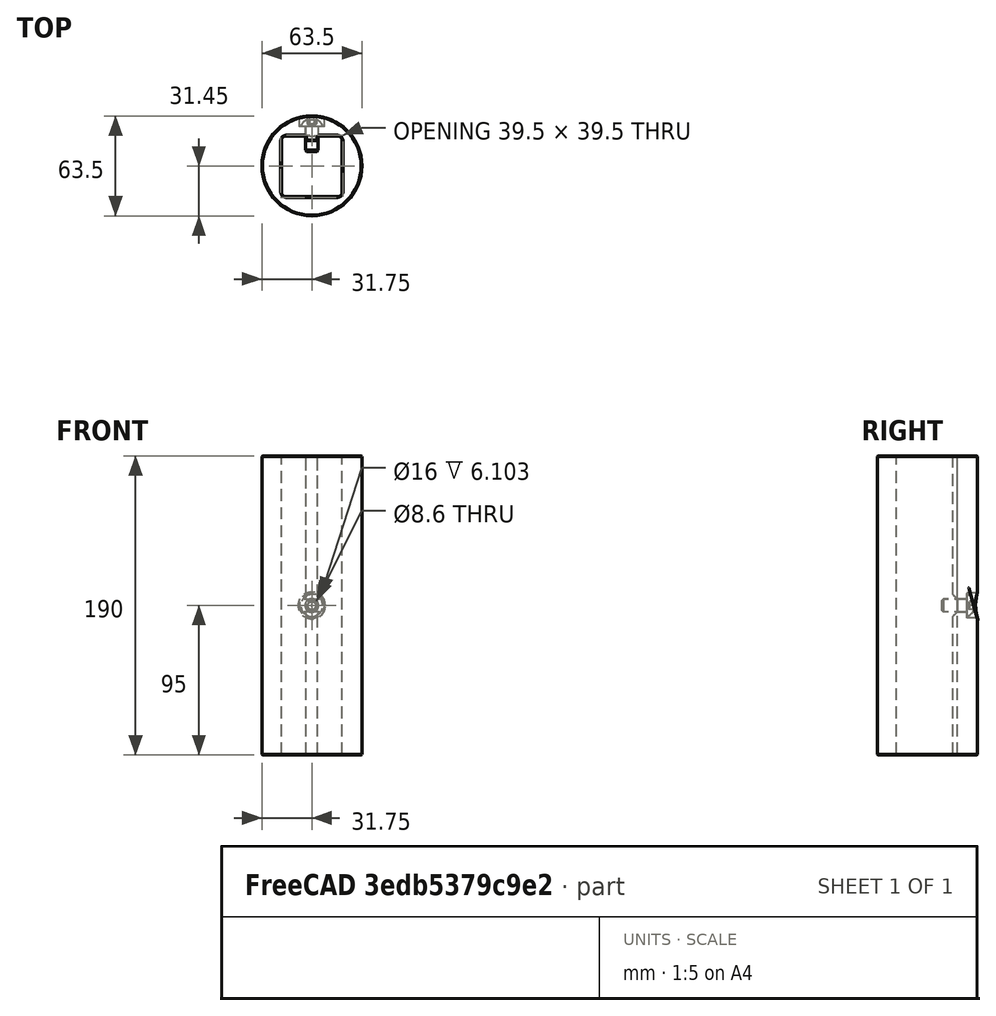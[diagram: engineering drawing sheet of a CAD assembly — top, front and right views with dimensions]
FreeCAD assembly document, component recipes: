
FREECAD ASSEMBLY — COMPONENT RECIPES ("bar-cover")

This assembly document has 3 components, labeled P0..P2 below (a component is one placed body or linked part). 2 of them carry a construction recipe — the FreeCAD feature program that regenerates the part from scratch, quoted from this document or its linked companion documents; the rest are supplied as boundary geometry only. No exploded tour is included for this assembly.
COMPONENT P0 — recipe-attached ("Bar Cover", modeled in this document).
Construction recipe (the document's own serialized feature program — sketch geometry with constraints, then the solid features built on it; lengths are millimeters unless a unit is written):

FEATURE [Sketcher::SketchObject] Sketch
  FullyConstrained = true
  MapMode = 5
  Support = -> [XY_Plane]
  expr: Constraints[19] = <<Configuration>>.extrusion_width + Spreadsheet.fit_tolerance * 2
  expr: Constraints[1] = <<Configuration>>.cover_outer_diameter
  expr: Constraints[28] = <<Configuration>>.slot_width - <<Configuration>>.fit_tolerance * 2
  expr: Constraints[36] = <<Configuration>>.slot_aligner_height
  expr: Constraints[39] = <<Configuration>>.extrusion_width / 2 + <<Configuration>>.fit_tolerance * 2
  expr: Constraints[40] = <<Configuration>>.extrusion_width / 2
  expr: Constraints[41] = <<Configuration>>.extrusion_corner_radius
  expr: Constraints[42] = <<Configuration>>.slot_corner_radius
  sketch-geometry (19):
    g0: Circle CenterX=0 CenterY=0 CenterZ=0 NormalX=0 NormalY=0 NormalZ=1 AngleXU=0 Radius=31.75
    g1: ArcOfCircle CenterX=-16.175 CenterY=15.875 CenterZ=0 NormalX=0 NormalY=0 NormalZ=1 AngleXU=0 Radius=3.175 StartAngle=1.5708 EndAngle=3.14159
    g2: LineSegment StartX=-16.175 StartY=19.05 StartZ=0 EndX=-5.035 EndY=19.05 EndZ=0
    g3: ArcOfCircle CenterX=16.175 CenterY=15.875 CenterZ=0 NormalX=0 NormalY=0 NormalZ=1 AngleXU=0 Radius=3.175 StartAngle=3e-16 EndAngle=1.5708
    g4: LineSegment StartX=19.35 StartY=15.875 StartZ=0 EndX=19.35 EndY=-16.475 EndZ=0
    g5: ArcOfCircle CenterX=16.175 CenterY=-16.475 CenterZ=0 NormalX=0 NormalY=0 NormalZ=1 AngleXU=0 Radius=3.175 StartAngle=4.71239 EndAngle=6.28319
    g6: LineSegment StartX=16.175 StartY=-19.65 StartZ=0 EndX=-16.175 EndY=-19.65 EndZ=0
    g7: ArcOfCircle CenterX=-16.175 CenterY=-16.475 CenterZ=0 NormalX=0 NormalY=0 NormalZ=1 AngleXU=0 Radius=3.175 StartAngle=3.14159 EndAngle=4.71239
    g8: LineSegment StartX=-19.35 StartY=-16.475 StartZ=0 EndX=-19.35 EndY=15.875 EndZ=0
    g9: GeomPoint X=-19.35 Y=19.05 Z=0
    g10: GeomPoint X=19.35 Y=-19.65 Z=0
    g11: LineSegment StartX=-3.765 StartY=17.78 StartZ=0 EndX=-3.765 EndY=17.05 EndZ=0
    g12: LineSegment StartX=-2.765 StartY=16.05 StartZ=0 EndX=2.765 EndY=16.05 EndZ=0
    g13: LineSegment StartX=3.765 StartY=17.05 StartZ=0 EndX=3.765 EndY=17.78 EndZ=0
    g14: LineSegment StartX=5.035 StartY=19.05 StartZ=0 EndX=16.175 EndY=19.05 EndZ=0
    g15: ArcOfCircle CenterX=-5.035 CenterY=17.78 CenterZ=0 NormalX=0 NormalY=0 NormalZ=1 AngleXU=0 Radius=1.27 StartAngle=7e-16 EndAngle=1.5708
    g16: ArcOfCircle CenterX=5.035 CenterY=17.78 CenterZ=0 NormalX=0 NormalY=0 NormalZ=1 AngleXU=0 Radius=1.27 StartAngle=1.5708 EndAngle=3.14159
    g17: ArcOfCircle CenterX=-2.765 CenterY=17.05 CenterZ=0 NormalX=0 NormalY=0 NormalZ=1 AngleXU=0 Radius=1 StartAngle=3.14159 EndAngle=4.71239
    g18: ArcOfCircle CenterX=2.765 CenterY=17.05 CenterZ=0 NormalX=0 NormalY=0 NormalZ=1 AngleXU=0 Radius=1 StartAngle=4.71239 EndAngle=6.28319
  constraints (43):
    c: Coincident(g0,g-1)
    c: Diameter(g0) = 63.5
    c: Tangent(g1,g2) = 1.5708
    c: Tangent(g3,g4) = 1.5708
    c: Tangent(g4,g5) = 1.5708
    c: Tangent(g5,g6) = 1.5708
    c: Tangent(g6,g7) = 1.5708
    c: Tangent(g7,g8) = 1.5708
    c: Tangent(g8,g1) = 1.5708
    c: Horizontal(g2)
    c: Horizontal(g6)
    c: Vertical(g4)
    c: Vertical(g8)
    c: Equal(g3,g5)
    c: Equal(g5,g7)
    c: PointOnObject(g9,g2)
    c: PointOnObject(g9,g8)
    c: PointOnObject(g10,g4)
    c: PointOnObject(g10,g6)
    c: DistanceX(g1,g3) = 38.7
    c: Vertical(g11)
    c: Vertical(g13)
    c: Tangent(g11,g15) = 1.5708
    c: Tangent(g2,g15) = 1.5708
    c: Tangent(g13,g16) = 1.5708
    c: Tangent(g14,g16) = 1.5708
    c: Equal(g16,g15)
    c: Tangent(g14,g2)
    c: DistanceX(g11,g13) = 7.53
    c: Tangent(g12,g17) = -1.5708
    c: Tangent(g11,g17) = -1.5708
    c: Tangent(g12,g18) = -1.5708
    c: Tangent(g13,g18) = -1.5708
    c: Equal(g17,g18)
    c: Diameter(g17) = 2
    c: Symmetric(g11,g13,g-2)
    c: DistanceY(g12,g2) = 3
    c: Tangent(g14,g3) = 1.5708
    c: Symmetric(g1,g3,g-2)
    c: DistanceY(g6,g-1) = 19.65
    c: DistanceY(g-1,g3) = 19.05
    c: Radius(g3) = 3.175
    c: Radius(g15) = 1.27
FEATURE [PartDesign::Pad] Pad
  Direction = (0,0,1)
  Length = 190
  Length2 = 10
  Profile = -> Sketch
  ReferenceAxis = -> Sketch [N_Axis]
  Type = 0
  expr: Length = <<Configuration>>.cover_length
FEATURE [Sketcher::SketchObject] Sketch001
  AttachmentOffset = pos=(0,0,-25.05) rot=(0,0,1;0rad)
  FullyConstrained = true
  MapMode = 5
  Placement = pos=(0,25.05,5.6e-15) rot=(1,0,0;1.5708rad)
  Support = -> [XZ_Plane]
  expr: .AttachmentOffset.Base.z = -(<<Configuration>>.extrusion_width / 2) - 6 mm
  expr: Constraints[1] = <<Configuration>>.screw_offset
  sketch-geometry (1):
    g0: Circle CenterX=0 CenterY=95 CenterZ=0 NormalX=0 NormalY=0 NormalZ=1 AngleXU=0 Radius=8
  constraints (3):
    c: PointOnObject(g0,g-2)
    c: DistanceY(g-1,g0) = 95
    c: Diameter(g0) = 16
FEATURE [PartDesign::Pocket] Pocket
  BaseFeature = -> Pad
  Direction = (0,1,2e-16)
  Length = 6.2
  Length2 = 5
  Profile = -> Sketch001
  ReferenceAxis = -> Sketch001 [N_Axis]
  Type = 1
FEATURE [Sketcher::SketchObject] Sketch002
  FullyConstrained = true
  MapMode = 5
  Placement = pos=(0,0,0) rot=(1,0,0;1.5708rad)
  Support = -> [XZ_Plane]
  expr: Constraints[1] = <<Configuration>>.screw_offset
  expr: Constraints[2] = 8 mm + <<Configuration>>.fit_tolerance * 2
  sketch-geometry (1):
    g0: Circle CenterX=0 CenterY=95 CenterZ=0 NormalX=0 NormalY=0 NormalZ=1 AngleXU=0 Radius=4.3
  constraints (3):
    c: PointOnObject(g0,g-2)
    c: DistanceY(g-1,g0) = 95
    c: Diameter(g0) = 8.6
FEATURE [PartDesign::Pocket] Pocket001
  BaseFeature = -> Pocket
  Direction = (0,1,2e-16)
  Length = 5
  Length2 = 5
  Profile = -> Sketch002
  ReferenceAxis = -> Sketch002 [N_Axis]
  Type = 1
FEATURE [Sketcher::SketchObject] Sketch003
  AttachmentOffset = pos=(0,19.05,95) rot=(-1,0,0;1.5708rad)
  FullyConstrained = true
  MapMode = 5
  Placement = pos=(0,19.05,95) rot=(-1,0,0;1.5708rad)
  Support = -> [XY_Plane]
  expr: .AttachmentOffset.Base.y = <<Configuration>>.extrusion_width / 2
  expr: .AttachmentOffset.Base.z = <<Configuration>>.screw_offset
  sketch-geometry (5):
    g0: LineSegment StartX=6 StartY=-4 StartZ=0 EndX=6 EndY=4 EndZ=0
    g1: LineSegment StartX=6 StartY=4 StartZ=0 EndX=-6 EndY=4 EndZ=0
    g2: LineSegment StartX=-6 StartY=4 StartZ=0 EndX=-6 EndY=-4 EndZ=0
    g3: LineSegment StartX=-6 StartY=-4 StartZ=0 EndX=6 EndY=-4 EndZ=0
    g4: GeomPoint X=0 Y=0 Z=0
  constraints (12):
    c: Coincident(g0,g1)
    c: Coincident(g1,g2)
    c: Coincident(g2,g3)
    c: Coincident(g3,g0)
    c: Horizontal(g1)
    c: Horizontal(g3)
    c: Vertical(g0)
    c: Vertical(g2)
    c: Symmetric(g1,g0,g4)
    c: Coincident(g4,g-1)
    c: DistanceX(g1,g1) = 12
    c: DistanceY(g2,g2) = 8
FEATURE [Sketcher::SketchObject] Sketch004
  AttachmentOffset = pos=(0,15.05,95) rot=(-1,0,0;1.5708rad)
  FullyConstrained = true
  MapMode = 5
  Placement = pos=(0,15.05,95) rot=(-1,0,0;1.5708rad)
  Support = -> [XY_Plane]
  expr: .AttachmentOffset.Base.y = <<Configuration>>.extrusion_width / 2 - <<Configuration>>.slot_aligner_height - 1 mm
  expr: .AttachmentOffset.Base.z = <<Configuration>>.screw_offset
  sketch-geometry (5):
    g0: LineSegment StartX=6 StartY=-8 StartZ=0 EndX=6 EndY=8 EndZ=0
    g1: LineSegment StartX=6 StartY=8 StartZ=0 EndX=-6 EndY=8 EndZ=0
    g2: LineSegment StartX=-6 StartY=8 StartZ=0 EndX=-6 EndY=-8 EndZ=0
    g3: LineSegment StartX=-6 StartY=-8 StartZ=0 EndX=6 EndY=-8 EndZ=0
    g4: GeomPoint X=0 Y=0 Z=0
  constraints (12):
    c: Coincident(g0,g1)
    c: Coincident(g1,g2)
    c: Coincident(g2,g3)
    c: Coincident(g3,g0)
    c: Horizontal(g1)
    c: Horizontal(g3)
    c: Vertical(g0)
    c: Vertical(g2)
    c: Symmetric(g1,g0,g4)
    c: Coincident(g4,g-1)
    c: DistanceX(g1,g1) = 12
    c: DistanceY(g2,g2) = 16
FEATURE [PartDesign::SubtractiveLoft] SubtractiveLoft
  BaseFeature = -> Pocket001
  Closed = false
  Profile = -> Sketch003
  Refine = true
  Ruled = false
  Sections = -> [Sketch004]
FEATURE [PartDesign::Chamfer] Chamfer
  Angle = 45
  Base = -> SubtractiveLoft [Face2,Face3]
  BaseFeature = -> SubtractiveLoft
  ChamferType = 0
  FlipDirection = false
  Refine = true
  Size = 0.4
  Size2 = 1
  SupportTransform = false
  UseAllEdges = false
FEATURE [PartDesign::Fillet] Fillet
  Base = -> Chamfer [Edge4]
  BaseFeature = -> Chamfer
  Radius = 0.6
  Refine = true
  SupportTransform = false
  UseAllEdges = false
FEATURE [PartDesign::Body] Body  label="BarCover"
  Group = -> [Sketch,Pad,Sketch001,Pocket,Sketch002,Pocket001,Sketch003,Sketch004,SubtractiveLoft,Chamfer,Fillet]
  Origin = -> Origin
  Tip = -> Fillet
COMPONENT P1 — recipe-attached ("1515 33.375", a linked part whose construction recipe lives in a companion FreeCAD document of the same project; that document's serialized recipe follows).
Construction recipe (the companion document, serialized — sketch geometry with constraints, then the solid features built on it; lengths are millimeters unless a unit is written):

FCSTD DOCUMENT  (FreeCAD 0.21R33668 +7 (Git))
Label: 1515-33.375
License: All rights reserved
LicenseURL: http://en.wikipedia.org/wiki/All_rights_reserved
objects: Sketcher::SketchObject×2, PartDesign::CoordinateSystem×1, PartDesign::Pad×1, PartDesign::Pocket×1, PartDesign::PolarPattern×1, PartDesign::Body×1, App::Part×1
note: 9 computed .brp shape members not serialized (recipe doc carries the construction recipe); baked Part::Feature solids carry a one-line shape summary decoded from their .brp

FEATURE [PartDesign::CoordinateSystem] LCS_001
  AttacherType = Attacher::AttachEngine3D
  MapMode = 2
  Support = -> [X_Axis001]
FEATURE [Sketcher::SketchObject] Sketch
  FullyConstrained = true
  MapMode = 5
  Placement = pos=(0,0,0) rot=(1,0,0;1.5708rad)
  Support = -> [XZ_Plane001]
  sketch-geometry (43):
    g0: ArcOfCircle CenterX=-15.87 CenterY=15.87 CenterZ=0 NormalX=0 NormalY=0 NormalZ=1 AngleXU=0 Radius=3.18 StartAngle=1.5708 EndAngle=3.14159
    g1: LineSegment StartX=-15.87 StartY=19.05 StartZ=0 EndX=15.87 EndY=19.05 EndZ=0
    g2: ArcOfCircle CenterX=15.87 CenterY=15.87 CenterZ=0 NormalX=0 NormalY=0 NormalZ=1 AngleXU=0 Radius=3.18 StartAngle=1e-16 EndAngle=1.5708
    g3: LineSegment StartX=19.05 StartY=15.87 StartZ=0 EndX=19.05 EndY=-15.87 EndZ=0
    g4: ArcOfCircle CenterX=15.87 CenterY=-15.87 CenterZ=0 NormalX=0 NormalY=0 NormalZ=1 AngleXU=0 Radius=3.18 StartAngle=4.71239 EndAngle=6.28319
    g5: LineSegment StartX=15.87 StartY=-19.05 StartZ=0 EndX=-15.87 EndY=-19.05 EndZ=0
    g6: ArcOfCircle CenterX=-15.87 CenterY=-15.87 CenterZ=0 NormalX=0 NormalY=0 NormalZ=1 AngleXU=0 Radius=3.18 StartAngle=3.14159 EndAngle=4.71239
    g7: LineSegment StartX=-19.05 StartY=-15.87 StartZ=0 EndX=-19.05 EndY=15.87 EndZ=0
    g8: GeomPoint X=-19.05 Y=19.05 Z=0
    g9: GeomPoint X=19.05 Y=-19.05 Z=0
    g10: LineSegment StartX=-12.145 StartY=-11.895 StartZ=0 EndX=-17.025 EndY=-11.895 EndZ=0
    g11: LineSegment StartX=-17.275 StartY=-12.145 StartZ=0 EndX=-17.275 EndY=-14.485 EndZ=0
    g12: LineSegment StartX=-14.485 StartY=-17.275 StartZ=0 EndX=-12.145 EndY=-17.275 EndZ=0
    g13: LineSegment StartX=-11.895 StartY=-17.025 StartZ=0 EndX=-11.895 EndY=-12.145 EndZ=0
    g14: ArcOfCircle CenterX=-14.485 CenterY=-14.485 CenterZ=0 NormalX=0 NormalY=0 NormalZ=1 AngleXU=0 Radius=2.79 StartAngle=3.14159 EndAngle=4.71239
    g15: LineSegment StartX=-12.145 StartY=11.895 StartZ=0 EndX=-17.025 EndY=11.895 EndZ=0
    g16: LineSegment StartX=-17.275 StartY=12.145 StartZ=0 EndX=-17.275 EndY=14.485 EndZ=0
    g17: ArcOfCircle CenterX=-14.485 CenterY=14.485 CenterZ=0 NormalX=0 NormalY=0 NormalZ=1 AngleXU=0 Radius=2.79 StartAngle=1.5708 EndAngle=3.14159
    g18: LineSegment StartX=-14.485 StartY=17.275 StartZ=0 EndX=-12.145 EndY=17.275 EndZ=0
    g19: LineSegment StartX=-11.895 StartY=17.025 StartZ=0 EndX=-11.895 EndY=12.145 EndZ=0
    g20: LineSegment StartX=12.145 StartY=11.895 StartZ=0 EndX=17.025 EndY=11.895 EndZ=0
    g21: LineSegment StartX=17.275 StartY=12.145 StartZ=0 EndX=17.275 EndY=14.485 EndZ=0
    g22: ArcOfCircle CenterX=14.485 CenterY=14.485 CenterZ=0 NormalX=0 NormalY=0 NormalZ=1 AngleXU=0 Radius=2.79 StartAngle=1e-16 EndAngle=1.5708
    g23: LineSegment StartX=14.485 StartY=17.275 StartZ=0 EndX=12.145 EndY=17.275 EndZ=0
    g24: LineSegment StartX=11.895 StartY=17.025 StartZ=0 EndX=11.895 EndY=12.145 EndZ=0
    g25: LineSegment StartX=12.145 StartY=-11.895 StartZ=0 EndX=17.025 EndY=-11.895 EndZ=0
    g26: LineSegment StartX=17.275 StartY=-12.145 StartZ=0 EndX=17.275 EndY=-14.485 EndZ=0
    g27: LineSegment StartX=14.485 StartY=-17.275 StartZ=0 EndX=12.145 EndY=-17.275 EndZ=0
    g28: LineSegment StartX=11.895 StartY=-17.025 StartZ=0 EndX=11.895 EndY=-12.145 EndZ=0
    g29: ArcOfCircle CenterX=14.485 CenterY=-14.485 CenterZ=0 NormalX=0 NormalY=0 NormalZ=1 AngleXU=0 Radius=2.79 StartAngle=4.71239 EndAngle=6.28319
    g30: Circle CenterX=0 CenterY=0 CenterZ=0 NormalX=0 NormalY=0 NormalZ=1 AngleXU=0 Radius=3.265
    g31: ArcOfCircle CenterX=-17.025 CenterY=-12.145 CenterZ=0 NormalX=0 NormalY=0 NormalZ=1 AngleXU=0 Radius=0.25 StartAngle=1.5708 EndAngle=3.14159
    g32: ArcOfCircle CenterX=-12.145 CenterY=-12.145 CenterZ=0 NormalX=0 NormalY=0 NormalZ=1 AngleXU=0 Radius=0.25 StartAngle=3.4e-15 EndAngle=1.5708
    g33: ArcOfCircle CenterX=-12.145 CenterY=-17.025 CenterZ=0 NormalX=0 NormalY=0 NormalZ=1 AngleXU=0 Radius=0.25 StartAngle=4.71239 EndAngle=6.28319
    g34: ArcOfCircle CenterX=-12.145 CenterY=17.025 CenterZ=0 NormalX=0 NormalY=0 NormalZ=1 AngleXU=0 Radius=0.25 StartAngle=1.4e-15 EndAngle=1.5708
    g35: ArcOfCircle CenterX=-12.145 CenterY=12.145 CenterZ=0 NormalX=0 NormalY=0 NormalZ=1 AngleXU=0 Radius=0.25 StartAngle=4.71239 EndAngle=6.28319
    g36: ArcOfCircle CenterX=-17.025 CenterY=12.145 CenterZ=0 NormalX=0 NormalY=0 NormalZ=1 AngleXU=0 Radius=0.25 StartAngle=3.14159 EndAngle=4.71239
    g37: ArcOfCircle CenterX=12.145 CenterY=17.025 CenterZ=0 NormalX=0 NormalY=0 NormalZ=1 AngleXU=0 Radius=0.25 StartAngle=1.5708 EndAngle=3.14159
    g38: ArcOfCircle CenterX=12.145 CenterY=12.145 CenterZ=0 NormalX=0 NormalY=0 NormalZ=1 AngleXU=0 Radius=0.25 StartAngle=3.14159 EndAngle=4.71239
    g39: ArcOfCircle CenterX=17.025 CenterY=12.145 CenterZ=0 NormalX=0 NormalY=0 NormalZ=1 AngleXU=0 Radius=0.25 StartAngle=4.71239 EndAngle=6.28319
    g40: ArcOfCircle CenterX=17.025 CenterY=-12.145 CenterZ=0 NormalX=0 NormalY=0 NormalZ=1 AngleXU=0 Radius=0.25 StartAngle=2.8e-15 EndAngle=1.5708
    g41: ArcOfCircle CenterX=12.145 CenterY=-12.145 CenterZ=0 NormalX=0 NormalY=0 NormalZ=1 AngleXU=0 Radius=0.25 StartAngle=1.5708 EndAngle=3.14159
    g42: ArcOfCircle CenterX=12.145 CenterY=-17.025 CenterZ=0 NormalX=0 NormalY=0 NormalZ=1 AngleXU=0 Radius=0.25 StartAngle=3.14159 EndAngle=4.71239
  constraints (101):
    c: Tangent(g0,g1) = 1.5708
    c: Tangent(g1,g2) = 1.5708
    c: Tangent(g2,g3) = 1.5708
    c: Tangent(g3,g4) = 1.5708
    c: Tangent(g4,g5) = 1.5708
    c: Tangent(g5,g6) = 1.5708
    c: Tangent(g6,g7) = 1.5708
    c: Tangent(g7,g0) = 1.5708
    c: Horizontal(g1)
    c: Horizontal(g5)
    c: Vertical(g3)
    c: Vertical(g7)
    c: Equal(g0,g2)
    c: Equal(g2,g4)
    c: Equal(g4,g6)
    c: PointOnObject(g8,g1)
    c: PointOnObject(g8,g7)
    c: PointOnObject(g9,g3)
    c: PointOnObject(g9,g5)
    c: Symmetric(g0,g4,g-1)
    c: Equal(g1,g3)
    c: DistanceX(g0,g2) = 38.1
    c: Horizontal(g10)
    c: Horizontal(g12)
    c: Vertical(g11)
    c: Vertical(g13)
    c: Tangent(g12,g14) = -1.5708
    c: Tangent(g11,g14) = -1.5708
    c: Horizontal(g15)
    c: Horizontal(g18)
    c: Vertical(g16)
    c: Vertical(g19)
    c: Tangent(g18,g17) = 1.5708
    c: Tangent(g16,g17) = 1.5708
    c: Horizontal(g25)
    c: Horizontal(g27)
    c: Vertical(g26)
    c: Vertical(g28)
    c: Tangent(g27,g29) = 1.5708
    c: Tangent(g26,g29) = 1.5708
    c: Horizontal(g20)
    c: Horizontal(g23)
    c: Vertical(g21)
    c: Tangent(g23,g22) = -1.5708
    c: Tangent(g21,g22) = -1.5708
    c: Coincident(g30,g-1)
    c: Diameter(g30) = 6.53
    c: Equal(g17,g22)
    c: Equal(g22,g29)
    c: Equal(g29,g14)
    c: Equal(g19,g15)
    c: Equal(g15,g24)
    c: Equal(g24,g20)
    c: Equal(g20,g25)
    c: Equal(g25,g28)
    c: Equal(g28,g13)
    c: Equal(g13,g10)
    c: Radius(g2) = 3.18
    c: Radius(g14) = 2.79
    c: Tangent(g11,g31) = -1.5708
    c: Tangent(g10,g31) = -1.5708
    c: Tangent(g13,g32) = -1.5708
    c: Tangent(g10,g32) = -1.5708
    c: Tangent(g13,g33) = -1.5708
    c: Tangent(g12,g33) = -1.5708
    c: Tangent(g18,g34) = 1.5708
    c: Tangent(g19,g34) = 1.5708
    c: Tangent(g19,g35) = 1.5708
    c: Tangent(g15,g35) = 1.5708
    c: Tangent(g15,g36) = 1.5708
    c: Tangent(g16,g36) = 1.5708
    c: Tangent(g23,g37) = -1.5708
    c: Tangent(g24,g37) = -1.5708
    c: Tangent(g20,g38) = -1.5708
    c: Tangent(g24,g38) = -1.5708
    c: Tangent(g21,g39) = -1.5708
    c: Tangent(g20,g39) = -1.5708
    c: Tangent(g26,g40) = 1.5708
    c: Tangent(g25,g40) = 1.5708
    c: Tangent(g28,g41) = 1.5708
    c: Tangent(g25,g41) = 1.5708
    c: Tangent(g27,g42) = 1.5708
    c: Tangent(g28,g42) = 1.5708
    c: Equal(g41,g40)
    c: Equal(g40,g42)
    c: Equal(g42,g32)
    c: Equal(g32,g33)
    c: Equal(g33,g31)
    c: Equal(g31,g34)
    c: Equal(g34,g35)
    c: Equal(g35,g36)
    c: Equal(g38,g39)
    c: Equal(g39,g37)
    c: Radius(g39) = 0.25
    c: DistanceX(g13,g28) = 23.79
    c: Symmetric(g13,g28,g-2)
    c: Symmetric(g10,g15,g-1)
    c: Symmetric(g19,g24,g-2)
    c: Symmetric(g20,g25,g-1)
    c: DistanceX(g11,g13) = 5.38
    c: DistanceY(g10,g15) = 23.79
FEATURE [PartDesign::Pad] Pad
  Direction = (0,-1,-2e-16)
  Length = 847.725
  Length2 = 10
  Placement = pos=(0,0,0) rot=(1,0,0;1.5708rad)
  Profile = -> Sketch
  ReferenceAxis = -> Sketch [N_Axis]
  Refine = true
  Type = 0
FEATURE [Sketcher::SketchObject] Sketch001  label="SlotSketch"
  FullyConstrained = true
  MapMode = 5
  Placement = pos=(0,0,0) rot=(1,0,0;1.5708rad)
  Support = -> [XZ_Plane001]
  sketch-geometry (34):
    g0: LineSegment StartX=-17.4444 StartY=4.065 StartZ=0 EndX=-15.9241 EndY=4.065 EndZ=0
    g1: LineSegment StartX=-14.6541 StartY=5.335 StartZ=0 EndX=-14.6541 EndY=6.61 EndZ=0
    g2: LineSegment StartX=-14.9041 StartY=6.86 StartZ=0 EndX=-15.2541 EndY=6.86 EndZ=0
    g3: LineSegment StartX=-15.5041 StartY=7.10389 StartZ=0 EndX=-15.55 EndY=8.98397 EndZ=0
    g4: LineSegment StartX=-14.2804 StartY=10.285 StartZ=0 EndX=-12.5452 EndY=10.285 EndZ=0
    g5: LineSegment StartX=-12.3685 StartY=10.2118 StartZ=0 EndX=-7.91157 EndY=5.7549 EndZ=0
    g6: ArcOfCircle CenterX=-15.9241 CenterY=5.335 CenterZ=0 NormalX=0 NormalY=0 NormalZ=1 AngleXU=0 Radius=1.27 StartAngle=4.71239 EndAngle=6.28319
    g7: ArcOfCircle CenterX=-14.9041 CenterY=6.61 CenterZ=0 NormalX=0 NormalY=0 NormalZ=1 AngleXU=0 Radius=0.25 StartAngle=6e-16 EndAngle=1.5708
    g8: ArcOfCircle CenterX=-15.2541 CenterY=7.11 CenterZ=0 NormalX=0 NormalY=0 NormalZ=1 AngleXU=0 Radius=0.25 StartAngle=3.16603 EndAngle=4.71239
    g9: ArcOfCircle CenterX=-14.2804 CenterY=9.015 CenterZ=0 NormalX=0 NormalY=0 NormalZ=1 AngleXU=0 Radius=1.27 StartAngle=1.5708 EndAngle=3.16603
    g10: ArcOfCircle CenterX=-12.5452 CenterY=10.035 CenterZ=0 NormalX=0 NormalY=0 NormalZ=1 AngleXU=0 Radius=0.25 StartAngle=0.785398 EndAngle=1.5708
    g11: LineSegment StartX=-14.6541 StartY=-5.335 StartZ=0 EndX=-14.6541 EndY=-6.61 EndZ=0
    g12: LineSegment StartX=-14.9041 StartY=-6.86 StartZ=0 EndX=-15.2541 EndY=-6.86 EndZ=0
    g13: LineSegment StartX=-15.5041 StartY=-7.10389 StartZ=0 EndX=-15.55 EndY=-8.98397 EndZ=0
    g14: LineSegment StartX=-14.2804 StartY=-10.285 StartZ=0 EndX=-12.5452 EndY=-10.285 EndZ=0
    g15: LineSegment StartX=-12.3685 StartY=-10.2118 StartZ=0 EndX=-7.91157 EndY=-5.7549 EndZ=0
    g16: ArcOfCircle CenterX=-15.9241 CenterY=-5.335 CenterZ=0 NormalX=0 NormalY=0 NormalZ=1 AngleXU=0 Radius=1.27 StartAngle=-9e-16 EndAngle=1.5708
    g17: ArcOfCircle CenterX=-14.9041 CenterY=-6.61 CenterZ=0 NormalX=0 NormalY=0 NormalZ=1 AngleXU=0 Radius=0.25 StartAngle=4.71239 EndAngle=6.28319
    g18: ArcOfCircle CenterX=-15.2541 CenterY=-7.11 CenterZ=0 NormalX=0 NormalY=0 NormalZ=1 AngleXU=0 Radius=0.25 StartAngle=1.5708 EndAngle=3.11716
    g19: ArcOfCircle CenterX=-14.2804 CenterY=-9.015 CenterZ=0 NormalX=0 NormalY=0 NormalZ=1 AngleXU=0 Radius=1.27 StartAngle=3.11716 EndAngle=4.71239
    g20: ArcOfCircle CenterX=-12.5452 CenterY=-10.035 CenterZ=0 NormalX=0 NormalY=0 NormalZ=1 AngleXU=0 Radius=0.25 StartAngle=4.71239 EndAngle=5.49779
    g21: LineSegment StartX=-6.74 StartY=-2.92647 StartZ=0 EndX=-6.74 EndY=2.92647 EndZ=0
    g22: ArcOfCircle CenterX=-10.74 CenterY=2.92647 CenterZ=0 NormalX=0 NormalY=0 NormalZ=1 AngleXU=0 Radius=4 StartAngle=0 EndAngle=0.785398
    g23: ArcOfCircle CenterX=-10.74 CenterY=-2.92647 CenterZ=0 NormalX=0 NormalY=0 NormalZ=1 AngleXU=0 Radius=4 StartAngle=5.49779 EndAngle=6.28319
    g24: LineSegment StartX=0 StartY=0 StartZ=0 EndX=-14.2804 EndY=14.2804 EndZ=0
    g25: LineSegment StartX=-7.14019 StartY=7.14019 StartZ=0 EndX=-8.21853 EndY=6.06185 EndZ=0
    g26: LineSegment StartX=-18.7141 StartY=5.30397 StartZ=0 EndX=-19.05 EndY=19.05 EndZ=0
    g27: ArcOfCircle CenterX=-17.4444 CenterY=5.335 CenterZ=0 NormalX=0 NormalY=0 NormalZ=1 AngleXU=0 Radius=1.27 StartAngle=3.16603 EndAngle=4.71239
    g28: LineSegment StartX=-18.7141 StartY=-5.30397 StartZ=0 EndX=-19.05 EndY=-19.05 EndZ=0
    g29: ArcOfCircle CenterX=-17.4444 CenterY=-5.335 CenterZ=0 NormalX=0 NormalY=0 NormalZ=1 AngleXU=0 Radius=1.27 StartAngle=1.5708 EndAngle=3.11716
    g30: LineSegment StartX=-17.4444 StartY=-4.065 StartZ=0 EndX=-15.9241 EndY=-4.065 EndZ=0
    g31: LineSegment StartX=-19.05 StartY=19.05 StartZ=0 EndX=-24.05 EndY=19.05 EndZ=0
    g32: LineSegment StartX=-24.05 StartY=19.05 StartZ=0 EndX=-24.05 EndY=-19.05 EndZ=0
    g33: LineSegment StartX=-24.05 StartY=-19.05 StartZ=0 EndX=-19.05 EndY=-19.05 EndZ=0
  constraints (78):
    c: Horizontal(g0)
    c: Tangent(g1,g6) = -1.5708
    c: Tangent(g0,g6) = -1.5708
    c: Tangent(g2,g7) = -1.5708
    c: Tangent(g1,g7) = -1.5708
    c: Tangent(g3,g8) = 1.5708
    c: Tangent(g2,g8) = 1.5708
    c: Tangent(g3,g9) = 1.5708
    c: Tangent(g4,g9) = 1.5708
    c: Tangent(g4,g10) = 1.5708
    c: Tangent(g5,g10) = 1.5708
    c: Horizontal(g4)
    c: Vertical(g1)
    c: Tangent(g11,g16) = 1.5708
    c: Tangent(g12,g17) = 1.5708
    c: Tangent(g11,g17) = 1.5708
    c: Tangent(g13,g18) = -1.5708
    c: Tangent(g12,g18) = -1.5708
    c: Tangent(g13,g19) = -1.5708
    c: Tangent(g14,g19) = -1.5708
    c: Tangent(g14,g20) = -1.5708
    c: Tangent(g15,g20) = -1.5708
    c: Tangent(g5,g22) = 1.5708
    c: Tangent(g21,g22) = -1.5708
    c: Tangent(g15,g23) = -1.5708
    c: Tangent(g21,g23) = -1.5708
    c: Angle(g-1,g5) = 2.35619
    c: Symmetric(g21,g21,g-1)
    c: Symmetric(g5,g15,g-1)
    c: Symmetric(g4,g14,g-1)
    c: Symmetric(g14,g4,g-1)
    c: Symmetric(g3,g13,g-1)
    c: Symmetric(g1,g11,g-1)
    c: Symmetric(g1,g11,g-1)
    c: Symmetric(g2,g12,g-1)
    c: Radius(g9) = 1.27
    c: Coincident(g24,g-1)
    c: Parallel(g5,g24)
    c: Vertical(g4,g24)
    c: PointOnObject(g25,g5)
    c: Perpendicular(g24,g25)
    c: Symmetric(g24,g24,g25)
    c: Distance(g25) = 1.525
    c: DistanceY(g14,g4) = 20.57
    c: DistanceY(g12,g2) = 13.72
    c: Radius(g6) = 1.27
    c: Radius(g7) = 0.25
    c: Radius(g8) = 0.25
    c: DistanceX(g21,g24) = 6.74
    c: Horizontal(g2)
    c: Radius(g18) = 0.25
    c: Radius(g23) = 4
    c: Radius(g20) = 0.25
    c: Tangent(g0,g27) = -1.5708
    c: Tangent(g26,g27) = 1.5708
    c: Equal(g6,g27)
    c: Angle(g-2,g26) = 0.0244346
    c: Tangent(g30,g29) = 1.5708
    c: Tangent(g28,g29) = -1.5708
    c: Coincident(g30,g16)
    c: Equal(g29,g27)
    c: Symmetric(g0,g16,g-1)
    c: Symmetric(g29,g0,g-1)
    c: Angle(g-2,g28) = -0.0244346
    c: Coincident(g31,g26)
    c: Horizontal(g31)
    c: Coincident(g32,g31)
    c: Coincident(g33,g32)
    c: Coincident(g33,g28)
    c: Horizontal(g33)
    c: DistanceY(g29,g0) = 8.13
    c: DistanceX(g28,g13) = 3.21
    c: DistanceY(g32,g32) = 38.1
    c: Symmetric(g31,g32,g-1)
    c: DistanceX(g26,g-1) = 19.05
    c: DistanceX(g33,g33) = 5
    c: DistanceX(g28,g11) = 4.06
    c: Parallel(g3,g26)
FEATURE [PartDesign::Pocket] Pocket
  BaseFeature = -> Pad
  Direction = (0,1,2e-16)
  Length = 5
  Length2 = 5
  Placement = pos=(0,0,0) rot=(1,0,0;1.5708rad)
  Profile = -> Sketch001
  ReferenceAxis = -> Sketch001 [N_Axis]
  Refine = true
  Reversed = true
  Type = 1
FEATURE [PartDesign::PolarPattern] PolarPattern
  Angle = 360
  Axis = -> Sketch001 [N_Axis]
  BaseFeature = -> Pocket
  Occurrences = 4
  Originals = -> [Pocket]
  Placement = pos=(0,0,0) rot=(1,0,0;1.5708rad)
  Refine = true
FEATURE [PartDesign::Body] _515  label="1515"
  Group = -> [LCS_001,Sketch,Pad,Sketch001,Pocket,PolarPattern]
  Origin = -> Origin001
  Tip = -> PolarPattern
FEATURE [App::Part] _515_33_375  label="1515 33.375"
  Group = -> [_515]
  Origin = -> Origin
COMPONENT P2 — geometry summary ("40-4040 849"; no construction recipe available for this part):
  bounding box: 849.0 x 40.0 x 40.0 mm
  tessellated surface: 3,296 triangles
  volume: 554017 mm^3 (41% of its bounding box)
  symmetry: 2-fold rotationally symmetric about the x axis; 2-fold rotationally symmetric about the y axis; 4-fold rotationally symmetric about the z axis; mirror-symmetric across its x mid-plane, y mid-plane, z mid-plane
PROVENANCE & LICENSES
A FreeCAD (.FCStd) document from a public repository crawl; recipes are the document's own serialized feature recipes (and, for linked parts, companion documents' recipes).
License: isc.
